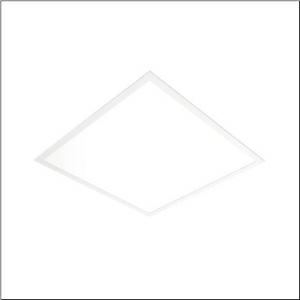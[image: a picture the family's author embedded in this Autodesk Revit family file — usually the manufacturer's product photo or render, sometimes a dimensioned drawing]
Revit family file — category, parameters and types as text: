
# Revit family: apollon_r__41_51mh12w72322_d90e
name_source: partatom
category: Lighting Fixtures
units: mm (PartAtom-declared; Revit-internal decimal feet)

## family parameters
Cut with Voids When Loaded = No
Host = Face
Light Source = No
Part Type = Normal
Room Calculation Point = No
Round Connector Dimension = Use Diameter
Shared = No

## types (1)
- Apollon® 41 (1 x LED, 3550 lm, 35 W, 3000K)
    Apparent Load = 35 VA
    CIE Flux Codes = 63 87 97 100 100
    Color Rendering = 80
    Color Temperature = 3000K
    Default Elevation = 1800 mm
    Description = Apollon® 41, office luminaire, primary optical cover: prismatic diffuser, of PS, light emission: direct distribution, primary light characteristic: symmetric, installation type: lay-in mounting, LED rated luminous flux: 3.550 lm, light colour: 830, colour temperature: 3000K, control gear: ECG, with terminal, 3-pole, mains connection: 220..240V, AC, 50/60Hz, rated input power: 35W, housing, of aluminium section, traffic white (RAL 9016), module: M600, length: 596 mm, width: 596 mm, height: 30mm, housing upper side, of sheet steel, protection rating (complete): IP20, protection rating (lamp compartment, on room side): IP40, insulation class (complete): insulation class II (safety insulation), certification: CE, ENEC, permissible ambient temperature for indoor applications: -20..+40°C, packaging unit: 1 piece
    Height = 0 mm  [stored 0 ft]
    Lamp = 1 x LED
    Lamp Light Flux = 3550 lm
    Lamp Power = 35 W
    Lamp count = 1
    Length = 595 mm
    Luminous efficacy = 101 lm/W
    Manufacturer = Siteco
    ModVariant = No
    Model = 51MH12W72322
    Mounting Place = Ceiling
    Mounting Type = Recessed
    Number of Poles = 1
    OnlyDefault = Yes
    Power Factor = 1
    Product Name = Apollon® 41
    Product group = office luminaire | ceiling recessed
    ProductGroupID = 400
    Protection Class = Protection class II
    Protection Degree = IP 20
    RLX_Detail_Level = 1
    RlxData = <blob elided: 14869 chars, md5=2d453722>
    Socket = socket
    Standby Power = 0 W
    System Light Flux = 3550 lm
    System Power = 35 W
    Type Comments = Product without accessories
    Type Image = l_1003755.jpg
    URL = http://relux.com
    VarID = ---
    Voltage = 0 V
    Weight = 0.00 kg
    Width = 595 mm

note: [stored X ft] marks values corroborated as IEEE doubles in the binary element streams (Revit-internal decimal feet)

## geometry (parser evidence)
native form markers: Sweep x11
no freeform markers — native parametric forms only
